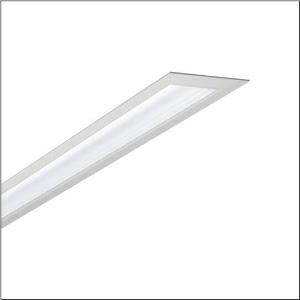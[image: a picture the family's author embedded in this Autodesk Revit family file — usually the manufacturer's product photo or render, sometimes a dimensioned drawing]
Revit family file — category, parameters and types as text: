
# Revit family: silica_r_5mx12wd1w4a_d237
name_source: partatom
category: Lighting Fixtures
units: mm (PartAtom-declared; Revit-internal decimal feet)

## family parameters
Cut with Voids When Loaded = No
Host = Face
Light Source = No
Part Type = Normal
Room Calculation Point = No
Round Connector Dimension = Use Diameter
Shared = No

## types (1)
- --- (1 x LED, 4680 lm, 29.3 W, 4000K)
    Apparent Load = 29 VA
    CIE Flux Codes = 70 95 99 100 100
    Color Rendering = 80
    Color Temperature = 4000K
    Default Elevation = 1800 mm
    Description = Silica®, office luminaire, primary light control with wallwasher, of aluminium, light emission: direct distribution, primary light characteristic: asymmetric, installation type: recessed, LED, rated luminous flux: 4.680lm, luminous efficacy: 160lm/W, light colour: 840, colour temperature: 4000K, control gear: DALI 2, with terminal, 3+2-pole, max. 2.5mm², mains connection: 230V, AC, 50/60Hz, rated input power: 29W, luminaire housing, of aluminium, matt pure white (RAL 9010), length: 1.462mm, width: 93mm, height: 60mm, end cap, of diecast zinc, pure white (RAL 9010), protection rating (complete): IP20, insulation class (complete): insulation class I (protective earthing), certification: CE, permissible operating ambient temperature: 0..+35°C, standard: EN 50419, packaging unit: 1 piece
    Height = 0 mm  [stored 0 ft]
    Lamp = 1 x LED
    Lamp Light Flux = 4680 lm
    Lamp Power = 29.3 W
    Lamp count = 1
    Length = 1462 mm
    Luminous efficacy = 160 lm/W
    Manufacturer = Siteco
    ModVariant = No
    Model = 5MX12WD1W4A
    Mounting Place = Ceiling
    Mounting Type = Recessed
    Number of Poles = 1
    OnlyDefault = Yes
    Power Factor = 1
    Product Name = Silica®
    Product group = office luminaire | ceiling recessed
    ProductGroupID = 401
    Protection Class = Protection class I
    Protection Degree = IP 20
    RLX_Detail_Level = 1
    RLX_Emergency_Light_Flux = 0 lm
    RLX_Emergency_Type = 0
    RLX_Emergency_Type_DB = No
    RlxData = <blob elided: 24581 chars, md5=d1dace90>
    Socket = socket
    Standby Power = 0 W
    System Light Flux = 4680 lm
    System Power = 29 W
    Type Comments = factory setting: luminous flux: 100 % | dim-lin: 254 | 164 mA
    Type Image = l_1004825.jpg
    URL = http://relux.com
    VarID = @adj_198553
    Voltage = 0 V
    Weight = 0.00 kg
    Width = 93 mm

note: [stored X ft] marks values corroborated as IEEE doubles in the binary element streams (Revit-internal decimal feet)

## geometry (parser evidence)
native form markers: Blend x4, Sweep x13
no freeform markers — native parametric forms only
